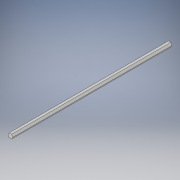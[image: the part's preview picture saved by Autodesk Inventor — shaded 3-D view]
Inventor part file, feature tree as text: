
AUTODESK INVENTOR PART (.ipt)
format: ipt  version: 2018 (Build 220112000, 112)  size: 96,768 bytes
history: native  units: in
note: dims shown in document units (in); Inventor stores cm internally (conversion verified against a paired STEP export)
features: extrude x1, sketch x1
ambient origin geometry x8: Origin, YZ Plane, XZ Plane, XY Plane, X Axis, Y Axis, Z Axis, Center Point
bodies: Solid1 (feature_tree)
feature tree (2):
  extrude  "Extrusion1"  Depth=19.0in TaperAngle=0.0deg
  sketch  "Sketch1"  dims[d0=0.25in d1=19.0in d2=0.0in]
